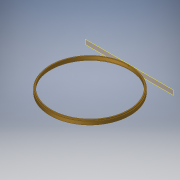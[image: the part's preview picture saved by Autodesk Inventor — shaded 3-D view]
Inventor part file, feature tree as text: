
AUTODESK INVENTOR PART (.ipt)
format: ipt  version: 2018 (Build 220112000, 112)  size: 162,304 bytes
history: native  units: in
note: dims shown in document units (in); Inventor stores cm internally (conversion verified against a paired STEP export)
features: sketch x4, extrude x3, plane x1, hole x1, pattern_circular x1
ambient origin geometry x8: Origin, YZ Plane, XZ Plane, XY Plane, X Axis, Y Axis, Z Axis, Center Point
bodies: Solid1 (feature_tree)
feature tree (10):
  extrude  "Extrusion1"  Depth=0.16in
  extrude  "Extrusion2"  Depth=0.095in
  plane  "Work Plane1"
  hole  "Hole1"  [1 undecoded]
  pattern_circular  "Circular Pattern1"  Count=6 Angle=360.0deg
  extrude  "Extrusion3"  Depth=0.125in
  sketch  "Sketch1"  dims[d0=7.75in d1=0.16in]
  sketch  "Sketch2"  dims[d2=0.325in d3=0.0in d4=0.095in]
  sketch  "Sketch3"  dims[d5=0.095in d6=0.0in d7=0.05in]
  sketch  "Sketch4"  dims[d8=0.062in d9=0.157in d10=0.375in d11=0.25in d12=0.5635in d13=0.248in d14=0.8108in d15=2.3622in d16=360.0deg d18=7.9in d19=0.125in d20=0.0in]
note: 1 required parameter value undecoded (feature->parameter linkage not recoverable at this tier; creation-order binding heuristic only, values carry confidence <= 0.55)
